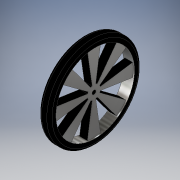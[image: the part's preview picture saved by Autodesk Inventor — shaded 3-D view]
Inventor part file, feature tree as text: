
AUTODESK INVENTOR PART (.ipt)
format: ipt  version: 2018 (Build 220112000, 112)  size: 217,088 bytes
history: native  units: in
note: dims shown in document units (in); Inventor stores cm internally (conversion verified against a paired STEP export)
features: extrude x4, sketch x4, fillet x1
ambient origin geometry x8: Origin, YZ Plane, XZ Plane, XY Plane, X Axis, Y Axis, Z Axis, Center Point
bodies: Solid1 (feature_tree)
feature tree (9):
  extrude  "Extrusion1"  Depth=2.3622in
  extrude  "Extrusion2"  Depth=0.3937in TaperAngle=360.0deg
  extrude  "Extrusion3"  Depth=0.0394in
  fillet  "Fillet1"  Radius=0.0394in
  extrude  "Extrusion4"  Depth=0.0787in
  sketch  "Sketch1"  dims[d0=2.7559in d1=2.3622in]
  sketch  "Sketch2"  dims[d2=0.3937in d3=3.1496in d5=360.0deg]
  sketch  "Sketch3"  dims[d7=0.315in d8=0.0in d9=2.3622in d10=0.0394in d11=0.0in]
  sketch  "Sketch4"  dims[d12=0.0394in d13=0.0in d14=0.0787in d15=0.1181in d16=0.3937in d17=0.0in]
